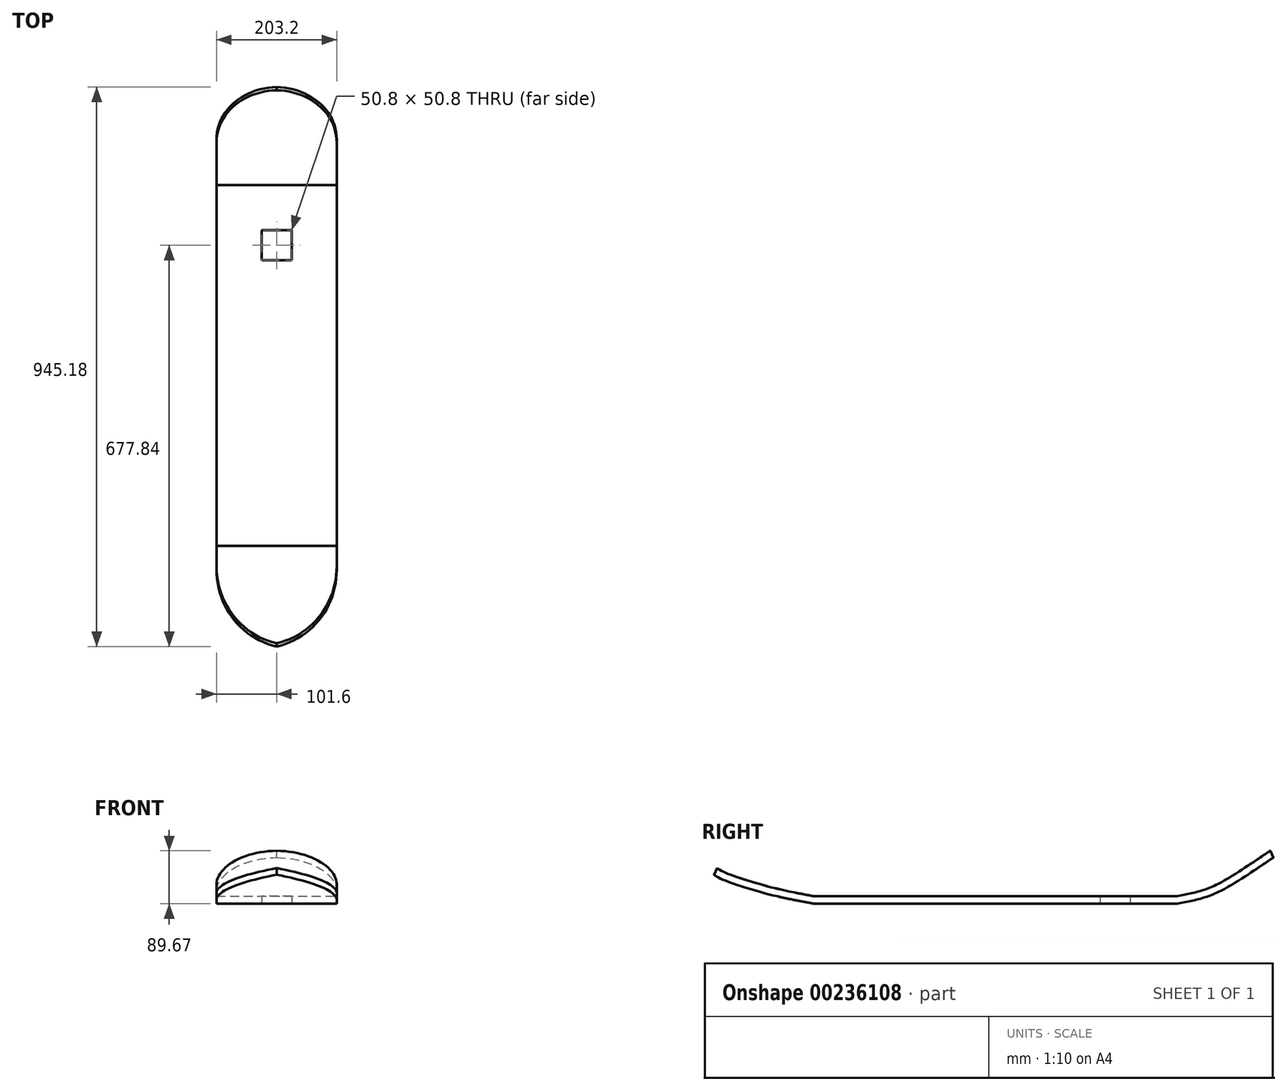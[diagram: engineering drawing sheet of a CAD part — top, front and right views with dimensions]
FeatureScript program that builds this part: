
annotation { "Feature Type Name" : "Feature", "Feature Type Description" : "" }
export const myFeature = defineFeature(function(context is Context, id is Id, definition is map)
    precondition{}
    {
        {
            var Q0;
            Q0=qCreatedBy(makeId("Top.planeOp"),FACE);
            var sketch = newSketch(context, id + "F0", { "sketchPlane" : qUnion([Q0])});
            skLineSegment(sketch, "E0.bottom", {"start": v(-101.6, -304.8) * mm, "end": v(101.6, -304.8) * mm});
            skLineSegment(sketch, "E0.top", {"start": v(-101.6, 304.8) * mm, "end": v(101.6, 304.8) * mm});
            skLineSegment(sketch, "E0.left", {"start": v(-101.6, -304.8) * mm, "end": v(-101.6, 304.8) * mm});
            skLineSegment(sketch, "E0.right", {"start": v(101.6, -304.8) * mm, "end": v(101.6, 304.8) * mm});
            skPoint(sketch, "E0.middle", {"position": v(0, 0) * mm});
            skLineSegment(sketch, "E1.bottom", {"start": v(25.4, 177.8) * mm, "end": v(-25.4, 177.8) * mm});
            skLineSegment(sketch, "E1.top", {"start": v(25.4, 228.6) * mm, "end": v(-25.4, 228.6) * mm});
            skLineSegment(sketch, "E1.left", {"start": v(25.4, 177.8) * mm, "end": v(25.4, 228.6) * mm});
            skLineSegment(sketch, "E1.right", {"start": v(-25.4, 177.8) * mm, "end": v(-25.4, 228.6) * mm});
            skPoint(sketch, "E1.middle", {"position": v(0, 203.2) * mm});
            skSolve(sketch);
        }
        {
            var Q0;
            Q0 = qSketchRegion(id + "F0", true);
            extrude(context, id + "F1", {"entities" : qUnion([Q0]), "endBound" : BoundingType.SYMMETRIC, "depth" : 12.7 * mm});
        }
        {
            var Q0;
            Q0=qCreatedBy(makeId("Right.planeOp"),FACE);
            var sketch = newSketch(context, id + "F2", { "sketchPlane" : qUnion([Q0])});
            skFitSpline(sketch, "E2", {"points": [v(306.4, 0) * mm, v(363.9, 14.22) * mm, v(426.13, 49.2) * mm, v(469.4, 78.23) * mm], "startDerivative": vector(172.94, 29.27) * mm, "endDerivative": vector(132.24, 89.85) * mm});
            skFitSpline(sketch, "E3", {"points": [v(-306.1, 0) * mm, v(-382.11, 16.07) * mm, v(-452.11, 37.9) * mm, v(-467.92, 45.42) * mm, v(-477.7, 52.2) * mm], "startDerivative": vector(-208.72, 38.61) * mm, "endDerivative": vector(-69.9, 51.08) * mm});
            skSolve(sketch);
        }
        {
            var Q0;
            Q0=makeQuery(id+"F1.opExtrude","SWEPT_FACE",FACE,{"disambiguationData":[OSD([sQuery(id+"F0.wireOp",EDGE,"E0.top")])]});
            var Q1;
            Q1=sQuery(id+"F2.wireOp",EDGE,"E2");
            sweep(context, id + "F3", {"operationType" : NewBodyOperationType.ADD, "profiles" : qUnion([Q0]), "path" : qUnion([Q1])});
        }
        {
            var Q0;
            Q0=makeQuery(id+"F1.opExtrude","SWEPT_FACE",FACE,{"disambiguationData":[OSD([sQuery(id+"F0.wireOp",EDGE,"E0.bottom")])]});
            var Q1;
            Q1=sQuery(id+"F2.wireOp",EDGE,"E3");
            sweep(context, id + "F4", {"operationType" : NewBodyOperationType.ADD, "profiles" : qUnion([Q0]), "path" : qUnion([Q1])});
        }
        {
            var Q0;
            Q0=makeQuery(id+"F4.opSweep","CAP_EDGE",EDGE,{"disambiguationData":[OSD([sQuery(id+"F0.wireOp",EDGE,"E0.bottom"),sQuery(id+"F0.wireOp",EDGE,"E0.left"),sQuery(id+"F2.wireOp",VERTEX,"E3.end")])],"isStart":false});
            var Q1;
            Q1=makeQuery(id+"F4.opSweep","CAP_EDGE",EDGE,{"disambiguationData":[OSD([sQuery(id+"F0.wireOp",EDGE,"E0.bottom"),sQuery(id+"F0.wireOp",EDGE,"E0.right"),sQuery(id+"F2.wireOp",VERTEX,"E3.end")])],"isStart":false});
            fillet(context, id + "F5", {"entities" : qUnion([Q0, Q1]), "radius" : 141.04 * mm, "tangentPropagation" : true, "allowEdgeOverflow" : false});
        }
        {
            var Q0;
            Q0=makeQuery(id+"F3.opSweep","CAP_EDGE",EDGE,{"disambiguationData":[OSD([sQuery(id+"F0.wireOp",EDGE,"E0.top"),sQuery(id+"F0.wireOp",EDGE,"E0.right"),sQuery(id+"F2.wireOp",VERTEX,"E2.end")])],"isStart":false});
            var Q1;
            Q1=makeQuery(id+"F3.opSweep","CAP_EDGE",EDGE,{"disambiguationData":[OSD([sQuery(id+"F0.wireOp",EDGE,"E0.top"),sQuery(id+"F0.wireOp",EDGE,"E0.left"),sQuery(id+"F2.wireOp",VERTEX,"E2.end")])],"isStart":false});
            fillet(context, id + "F6", {"entities" : qUnion([Q0, Q1]), "radius" : 104.25 * mm, "tangentPropagation" : true, "allowEdgeOverflow" : false});
        }
    });
